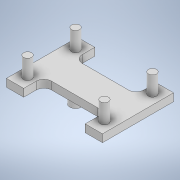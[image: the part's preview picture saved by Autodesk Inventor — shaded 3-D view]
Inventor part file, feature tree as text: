
AUTODESK INVENTOR PART (.ipt)
format: ipt  version: 2022.6 (Build 266554000, 554)  size: 155,648 bytes
history: native  units: mm
features: extrude x3, sketch x3, fillet x1
ambient origin geometry x8: Origin, YZ Plane, XZ Plane, XY Plane, X Axis, Y Axis, Z Axis, Center Point
bodies: Solid1 (feature_tree)
feature tree (7):
  extrude  "Extrusion1"  Depth=18.5mm
  extrude  "Extrusion2"  Depth=2.0mm
  extrude  "Extrusion4"  Depth=2.0mm
  fillet  "Fillet1"  Radius=5.0mm
  sketch  "Sketch1"  dims[d0=25.0mm d1=18.5mm]
  sketch  "Sketch2"  dims[d2=2.0mm d3=0.0mm d5=20.0mm]
  sketch  "Sketch5"  dims[d6=12.5mm d10=2.1mm d11=5.0mm d12=0.0mm d24=8.0mm d25=16.0mm d26=3.0mm d27=3.0mm d28=1.0mm d29=9.5mm d30=5.0mm d31=0.0mm d32=2.0mm]
